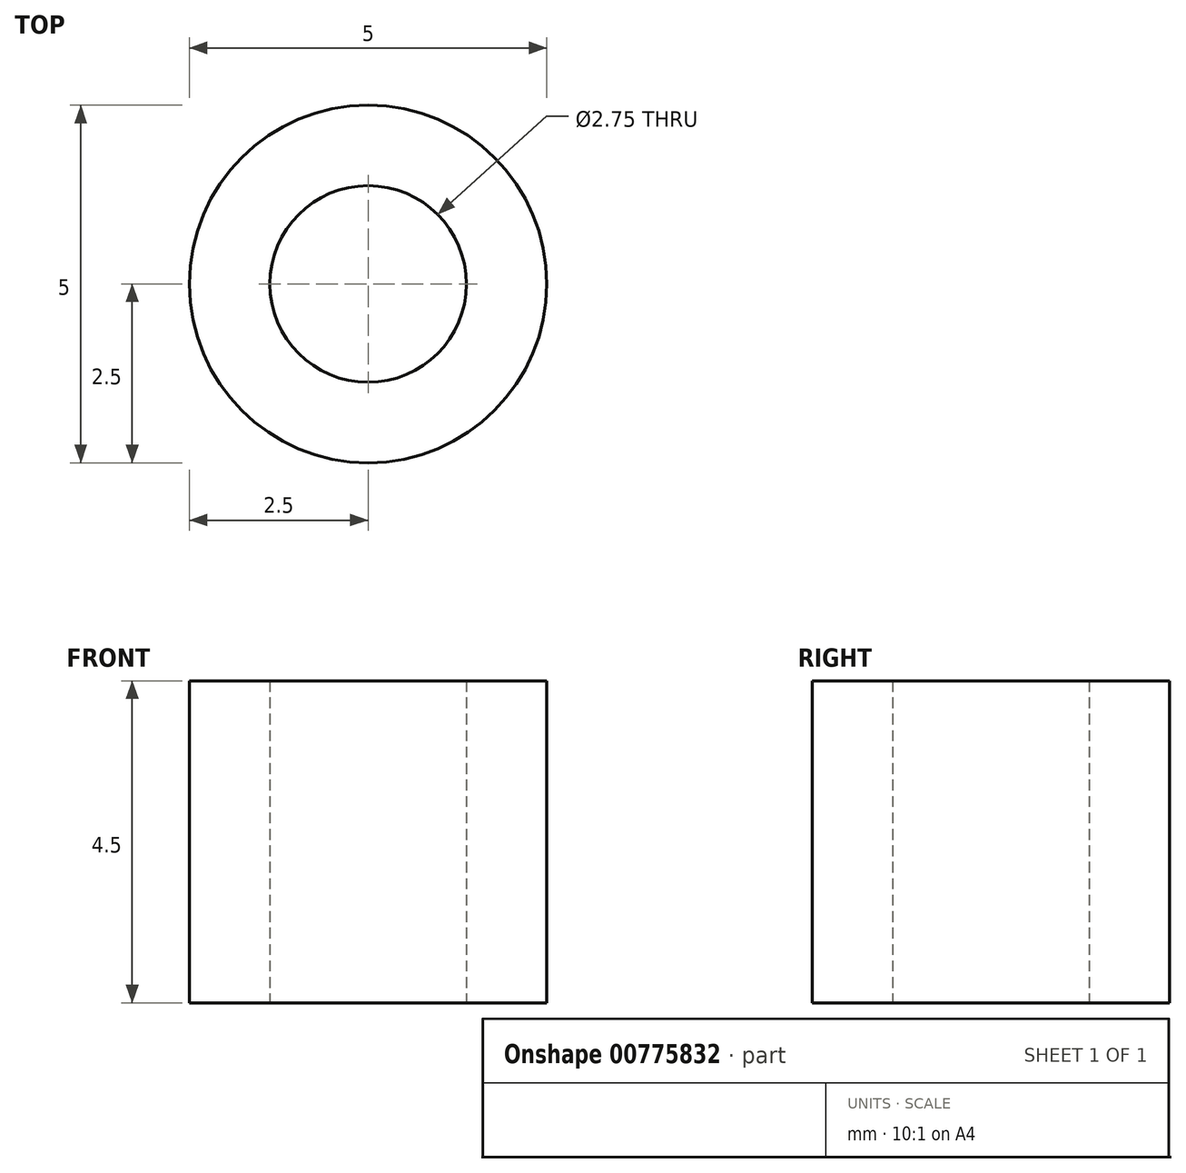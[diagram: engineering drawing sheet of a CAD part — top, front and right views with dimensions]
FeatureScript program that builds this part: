
annotation { "Feature Type Name" : "Feature", "Feature Type Description" : "" }
export const myFeature = defineFeature(function(context is Context, id is Id, definition is map)
    precondition{}
    {
        {
            assignVariable(context, id + "F0", {"name" : "SpacerHeight", "anyValue" : 4.5 * mm});
        }
        {
            var Q0;
            Q0=qCreatedBy(makeId("Top.planeOp"),FACE);
            var sketch = newSketch(context, id + "F1", { "sketchPlane" : qUnion([Q0])});
            skCircle(sketch, "E0", {"center": v(0, 0) * mm, "radius": 2.5 * mm});
            skCircle(sketch, "E1", {"center": v(0, 0) * mm, "radius": 1.37 * mm});
            skSolve(sketch);
        }
        {
            var Q0;
            Q0 = qSketchRegion(id + "F1", true);
            extrude(context, id + "F2", {"entities" : qUnion([Q0]), "depth" : getVariable(context, 'SpacerHeight'), "offsetDistance" : 25 * mm});
        }
    });
